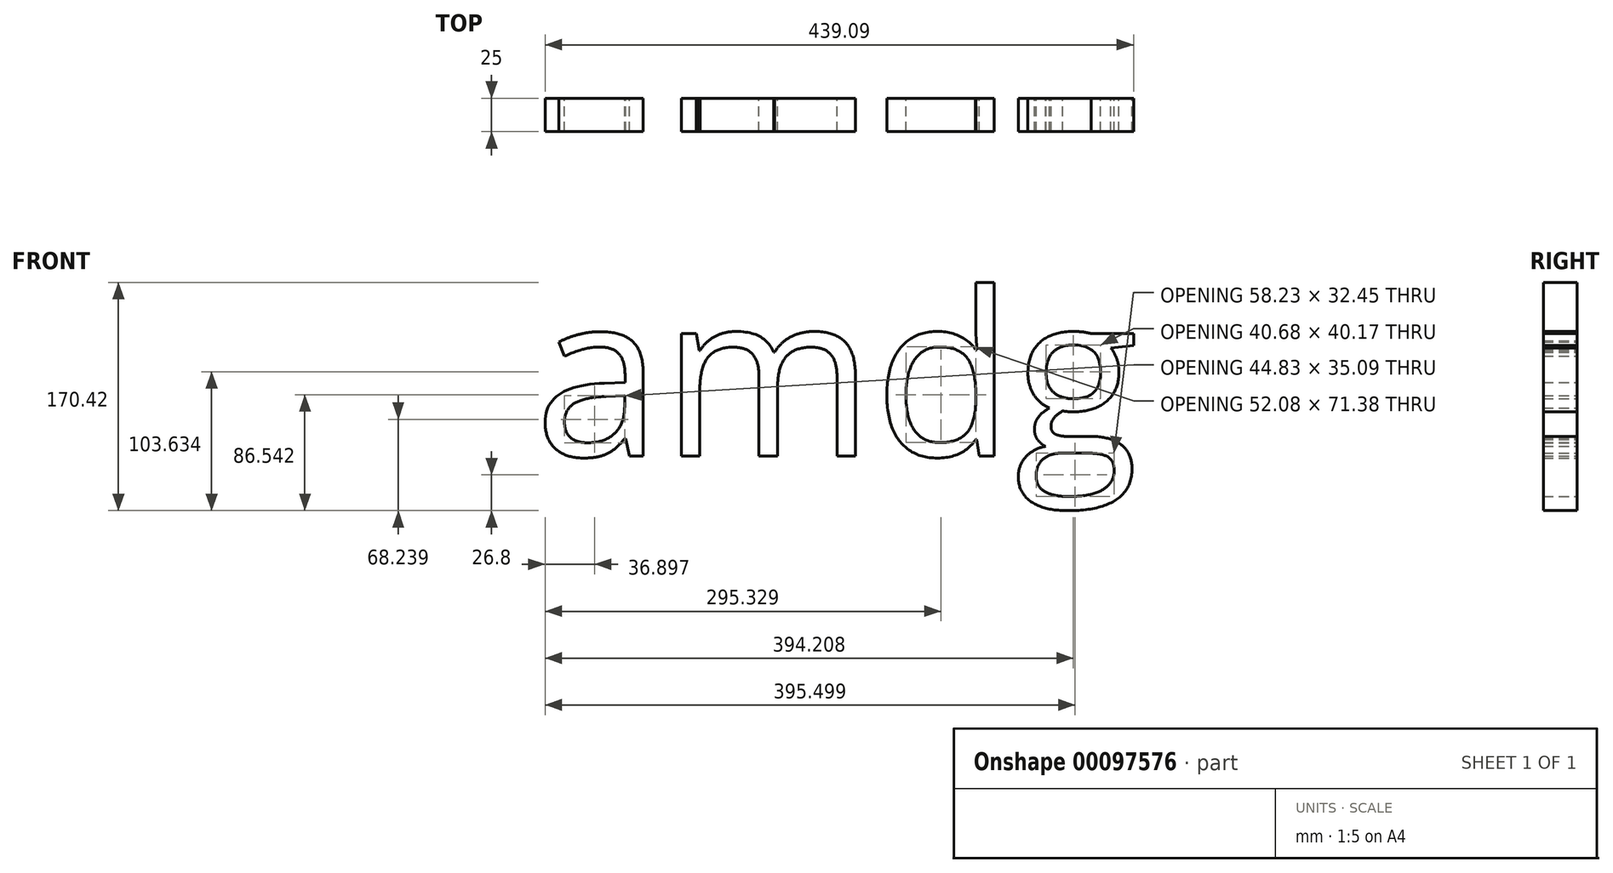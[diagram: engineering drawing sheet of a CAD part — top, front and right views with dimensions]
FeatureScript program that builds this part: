
annotation { "Feature Type Name" : "Feature", "Feature Type Description" : "" }
export const myFeature = defineFeature(function(context is Context, id is Id, definition is map)
    precondition{}
    {
        {
            var Q0;
            Q0=qCreatedBy(makeId("Front.planeOp"),FACE);
            var sketch = newSketch(context, id + "F0", { "sketchPlane" : qUnion([Q0])});
            skText(sketch, "E0", { "text": "amdg", "fontName": "OpenSans-Regular.ttf"});
            const initialGuessF0  = {"E0": [-0.09726, -0.01215, 1, 0, 0.12268]};
            skSetInitialGuess(sketch, initialGuessF0);
            skSolve(sketch);
        }
        {
            var Q0;
            Q0 = qSketchRegion(id + "F0", true);
            extrude(context, id + "F1", {"entities" : qUnion([Q0]), "depth" : 25 * mm});
        }
        {
            var Q0;
            Q0=makeQuery(id+"F1.opExtrude","SWEPT_FACE",FACE,{"disambiguationData":[OSD([sQuery(id+"F0.wireOp",EDGE,"E0.sketch_text.stroke-66")])]});
            var sketch = newSketch(context, id + "F2", { "sketchPlane" : qUnion([Q0])});
            skLineSegment(sketch, "E1", {"start": v(245.76, 0) * mm, "end": v(245.76, -25) * mm});
            skLineSegment(sketch, "E2", {"start": v(245.76, -25) * mm, "end": v(231.94, -25) * mm});
            skLineSegment(sketch, "E3", {"start": v(231.94, -25) * mm, "end": v(231.94, 0) * mm});
            skLineSegment(sketch, "E4", {"start": v(231.94, 0) * mm, "end": v(245.76, 0) * mm});
            skSolve(sketch);
        }
    });
